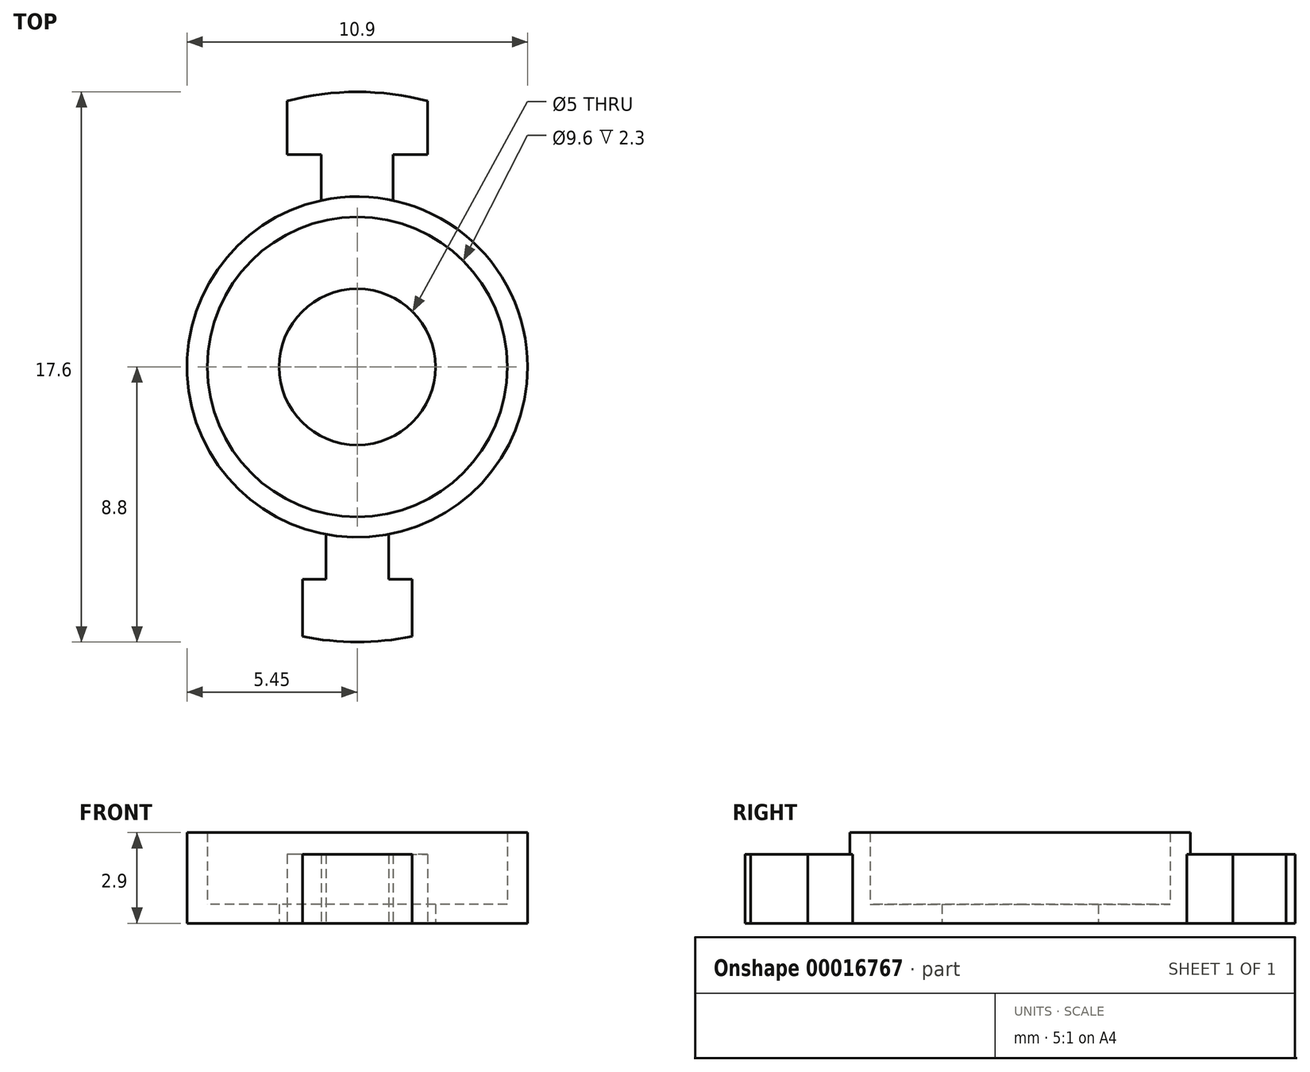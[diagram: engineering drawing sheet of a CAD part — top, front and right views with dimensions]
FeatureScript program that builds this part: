
annotation { "Feature Type Name" : "Feature", "Feature Type Description" : "" }
export const myFeature = defineFeature(function(context is Context, id is Id, definition is map)
    precondition{}
    {
        {
            var Q0;
            Q0=qCreatedBy(makeId("Top.planeOp"),FACE);
            var sketch = newSketch(context, id + "F0", { "sketchPlane" : qUnion([Q0])});
            skArc(sketch, "E0", {"start": v(0, -2.5) * mm, "mid": v(2.5, 0) * mm, "end": v(0, 2.5) * mm});
            skArc(sketch, "E1", {"start": v(0, -5.45) * mm, "mid": v(5.45, 0) * mm, "end": v(0, 5.45) * mm});
            skLineSegment(sketch, "E2", {"start": v(0, 5.45) * mm, "end": v(0, 2.5) * mm});
            skLineSegment(sketch, "E3.trimOffspring", {"start": v(0, -2.5) * mm, "end": v(0, -5.45) * mm});
            skSolve(sketch);
        }
        {
            var Q0;
            Q0=makeQuery(id+"F0.imprint","IMPRINT",FACE,{"disambiguationData":[TD([[makeQuery(id+"F0.imprint","IMPRINT",EDGE,{"derivedFrom":sQuery(id+"F0.wireOp",EDGE,"E0")}),-1.0]])]});
            extrude(context, id + "F1", {"entities" : qUnion([Q0]), "depth" : .6 * mm});
        }
        {
            var Q0;
            Q0=qCreatedBy(makeId("Top.planeOp"),FACE);
            var sketch = newSketch(context, id + "F2", { "sketchPlane" : qUnion([Q0])});
            skArc(sketch, "E4", {"start": v(0, -5.45) * mm, "mid": v(5.45, 0) * mm, "end": v(0, 5.45) * mm});
            skArc(sketch, "E5", {"start": v(0, -4.8) * mm, "mid": v(4.8, 0) * mm, "end": v(0, 4.8) * mm});
            skLineSegment(sketch, "E6", {"start": v(0, 5.45) * mm, "end": v(0, 4.8) * mm});
            skLineSegment(sketch, "E7.trimOffspring", {"start": v(0, -4.8) * mm, "end": v(0, -5.45) * mm});
            skSolve(sketch);
        }
        {
            var Q0;
            Q0=makeQuery(id+"F2.imprint","IMPRINT",FACE,{"disambiguationData":[TD([[makeQuery(id+"F2.imprint","IMPRINT",EDGE,{"derivedFrom":sQuery(id+"F2.wireOp",EDGE,"E4")}),1.0]])]});
            extrude(context, id + "F3", {"entities" : qUnion([Q0]), "operationType" : NewBodyOperationType.ADD, "depth" : 2.9 * mm});
        }
        {
            var Q0;
            Q0=qCreatedBy(makeId("Top.planeOp"),FACE);
            var sketch = newSketch(context, id + "F4", { "sketchPlane" : qUnion([Q0])});
            skLineSegment(sketch, "E8.bottom", {"start": v(0, 4.8) * mm, "end": v(1.15, 4.8) * mm});
            skLineSegment(sketch, "E8.left", {"start": v(0, 4.8) * mm, "end": v(0, 6.97) * mm});
            skLineSegment(sketch, "E8.right", {"start": v(1.15, 4.8) * mm, "end": v(1.15, 6.8) * mm});
            skLineSegment(sketch, "E9.left", {"start": v(0, 6.97) * mm, "end": v(0, 8.8) * mm});
            skLineSegment(sketch, "E9.right", {"start": v(2.25, 6.8) * mm, "end": v(2.25, 8.5) * mm});
            skLineSegment(sketch, "E10.bottom", {"start": v(0, -4.8) * mm, "end": v(1, -4.8) * mm});
            skLineSegment(sketch, "E10.left", {"start": v(0, -4.8) * mm, "end": v(0, -7.27) * mm});
            skLineSegment(sketch, "E10.right", {"start": v(1, -4.8) * mm, "end": v(1, -6.8) * mm});
            skLineSegment(sketch, "E11.left", {"start": v(0, -7.27) * mm, "end": v(0, -8.8) * mm});
            skLineSegment(sketch, "E11.right", {"start": v(1.75, -6.8) * mm, "end": v(1.75, -8.62) * mm});
            skLineSegment(sketch, "E12", {"start": v(1, -6.8) * mm, "end": v(1.75, -6.8) * mm});
            skLineSegment(sketch, "E13", {"start": v(1.15, 6.8) * mm, "end": v(2.25, 6.8) * mm});
            skLineSegment(sketch, "E14", {"start": v(0, -18.06) * mm, "end": v(0, -12.09) * mm, "construction": true});
            skArc(sketch, "E15", {"start": v(0, -8.8) * mm, "mid": v(8.8, 0) * mm, "end": v(0, 8.8) * mm});
            skSolve(sketch);
        }
        {
            var Q0;
            Q0=makeQuery(id+"F4.imprint","IMPRINT",FACE,{"disambiguationData":[TD([[makeQuery(id+"F4.imprint","IMPRINT",EDGE,{"derivedFrom":sQuery(id+"F4.wireOp",EDGE,"E8.bottom")}),1.0]])]});
            var Q1;
            Q1=makeQuery(id+"F4.imprint","IMPRINT",FACE,{"disambiguationData":[TD([[makeQuery(id+"F4.imprint","IMPRINT",EDGE,{"derivedFrom":sQuery(id+"F4.wireOp",EDGE,"E10.bottom")}),-1.0]])]});
            extrude(context, id + "F5", {"entities" : qUnion([Q0, Q1]), "operationType" : NewBodyOperationType.ADD, "depth" : 2.2 * mm});
        }
        {
            var Q0;
            Q0=makeQuery(id+"F1.opExtrude","SWEPT_BODY",BODY,{"disambiguationData":[OSD([sQuery(id+"F0.wireOp",EDGE,"E0"),sQuery(id+"F0.wireOp",EDGE,"E1"),sQuery(id+"F0.wireOp",EDGE,"E2"),sQuery(id+"F0.wireOp",EDGE,"E3.trimOffspring")])]});
            var Q1;
            Q1=makeQuery(id+"F5.boolean.opBoolean","MERGE",FACE,{"derivedFrom":[makeQuery(id+"F3.boolean.opBoolean","MERGE",FACE,{"derivedFrom":[makeQuery(id+"F1.opExtrude","SWEPT_FACE",FACE,{"disambiguationData":[OSD([sQuery(id+"F0.wireOp",EDGE,"E2")])]}),makeQuery(id+"F3.opExtrude","SWEPT_FACE",FACE,{"disambiguationData":[OSD([sQuery(id+"F2.wireOp",EDGE,"E6")])]})]}),makeQuery(id+"F5.opExtrude","SWEPT_FACE",FACE,{"disambiguationData":[OSD([sQuery(id+"F4.wireOp",EDGE,"E8.left"),sQuery(id+"F4.wireOp",EDGE,"E9.left")])]})]});
            mirror(context, id + "F6", {"operationType" : NewBodyOperationType.ADD, "entities" : qUnion([Q0]), "mirrorPlane" : qUnion([Q1])});
        }
    });
